# Revit family: Showerhead-American_Standard-Spectra_Traditional-9138073_Series
name_source: partatom
category: Plumbing Fixtures
units: mm (PartAtom-declared; Revit-internal decimal feet)

## family parameters
Always vertical = No
Cut with Voids When Loaded = No
OmniClass Number = 23.45.05.14.17
OmniClass Title = Showers
Part Type = Normal
Room Calculation Point = No
Round Connector Dimension = Use Diameter
Shared = Yes
Work Plane-Based = Yes

## types (5) — shared parameters
Assembly Code = D2010710
CW Connection = Yes
CWFU = 3
Default Elevation = 74"
Description = Spectra® Fixed™ Traditional 4-Function Showerhead
Diameter = 7 1/4"
Flow Rate = 1.8 gpm/6.8 L/min.
HW Connection = Yes
HWFU = 3
Height = 3 3/16"
IAPMO Compliance = Product meet or exceeds ASME A112.18.1,  CSA B125.1, EPA Water Sense
Installation Type = Wall Mounted
Manufacturer = American Standard
Max. Flow Rate = 1.8 gpm/6.8 L/min.
Price = Prices may vary. Please consult Manufacturer Representative for most up-to-date price list.
URL = https://www.americanstandard-us.com
Vent Connection = No
Waste Connection = No
Water Connection Diameter = 1/2"
Water Connection Radius = 1/4"
zero-valued in all types: WFU

## per-type parameters (varying)
| type | Finish | Material |
| 9138073.002 | Brass-American_Standard-002-Polished_Chrome | Brass-American_Standard-002-Polished_Chrome |
| 9138073.295 | Brass-American_Standard-295-Brushed_Nickel | Brass-American_Standard-295-Brushed_Nickel |
| 9138073.278 | Brass-American_Standard-278-Legacy_Bronze | Brass-American_Standard-278-Legacy_Bronze |
| 9138073.013 | Brass-American_Standard-013-Polished_Nickel | Brass-American_Standard-013-Polished_Nickel |
| 9138073.GN0 | Brass-American_Standard-GN0-Brushed_Cool_Sunrise | Brass-American_Standard-GN0-Brushed_Cool_Sunrise |

note: column(s) folded — value = type name in every type: Model

## geometry (parser evidence)
native form markers: Sweep x2
no freeform markers — native parametric forms only
